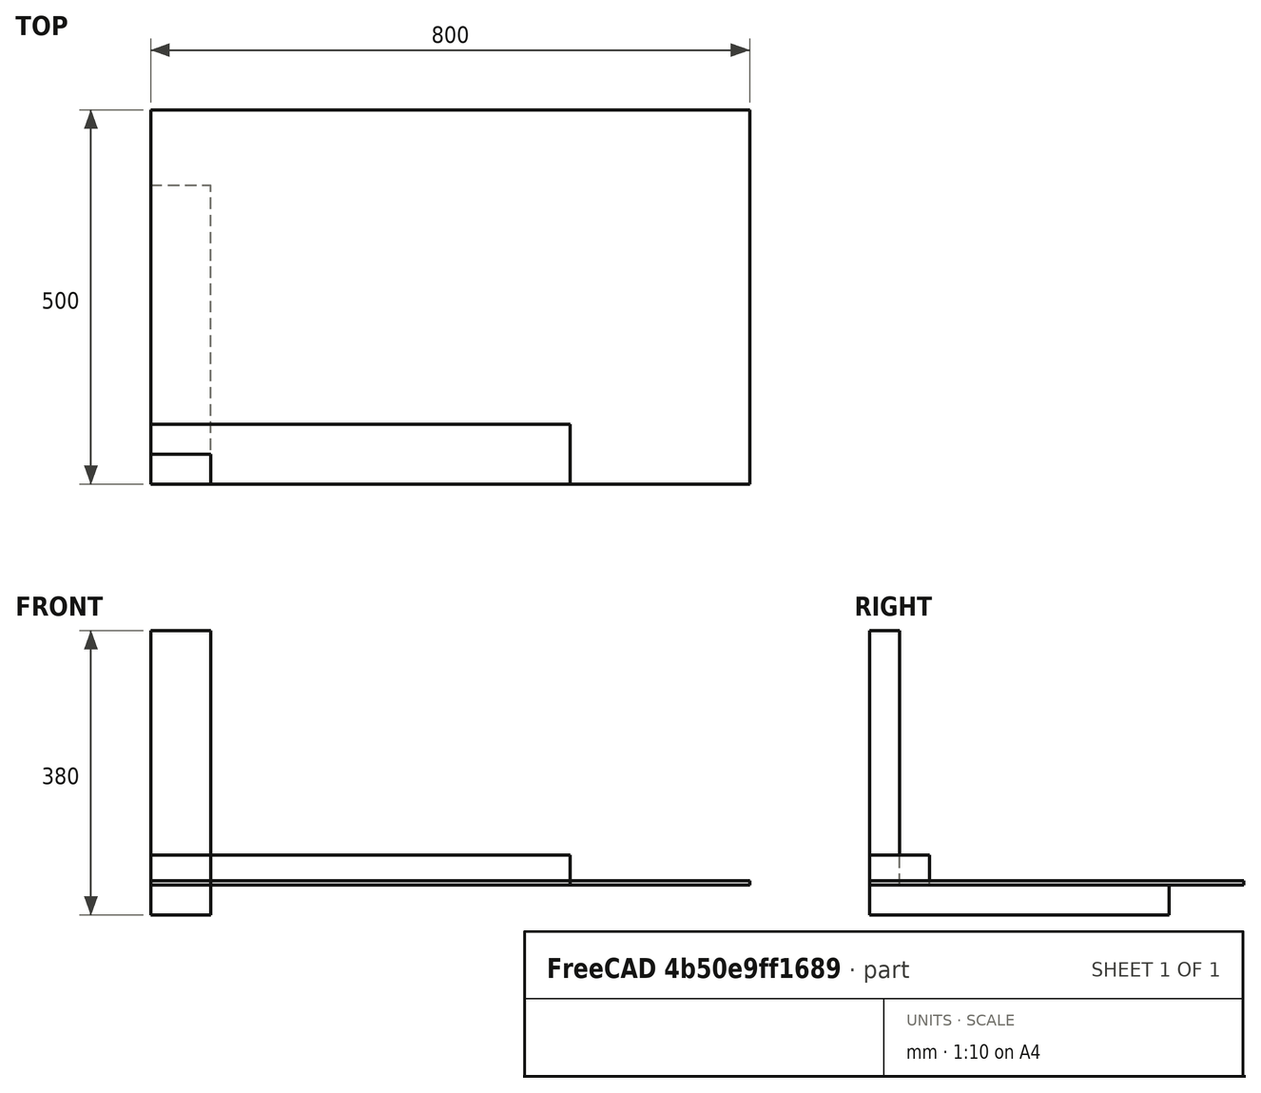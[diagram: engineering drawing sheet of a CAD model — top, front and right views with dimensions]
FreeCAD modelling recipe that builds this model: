
FCSTD DOCUMENT  (FreeCAD 0.21R33694 (Git))
Label: Lumber_coffe_table
Comment: Parametric design with spreadsheet.
License: Creative Commons Attribution-NonCommercial-ShareAlike 4.0
LicenseURL: https://creativecommons.org/licenses/by-nc-sa/4.0/
objects: PartDesign::AdditiveBox×4, PartDesign::Body×4, App::Link×4, App::Part×4, Spreadsheet::Sheet×1
note: 12 computed .brp shape members not serialized (recipe doc carries the construction recipe); baked Part::Feature solids carry a one-line shape summary decoded from their .brp

FEATURE [PartDesign::AdditiveBox] Box
  AttacherType = Attacher::AttachEngine3D
  Height = 340
  Length = 80
  MapMode = 1
  Width = 40
  expr: Height = Spreadsheet.l_v
  expr: Length = Spreadsheet.ancho
  expr: Width = Spreadsheet.grosor
FEATURE [PartDesign::Body] Body  label="Madera_300"
  Group = -> [Box]
  Origin = -> Origin001
  Tip = -> Box
FEATURE [PartDesign::AdditiveBox] Box001
  AttacherType = Attacher::AttachEngine3D
  Height = 400
  Length = 80
  Width = 40
  expr: Height = Spreadsheet.l_h
  expr: Length = Spreadsheet.ancho
  expr: Width = Spreadsheet.grosor
FEATURE [PartDesign::Body] Body001  label="Madera_500"
  Group = -> [Box001]
  Origin = -> Origin002
  Placement = pos=(0,0,0) rot=(-1,0,0;1.5708rad)
  Tip = -> Box001
FEATURE [App::Link] Link  label="Madera_501"
  LinkPlacement = pos=(0,0,380) rot=(0,0,1;0rad)
  LinkTransform = true
  LinkedObject = -> Body001
  Placement = pos=(0,0,380) rot=(0,0,1;0rad)
  expr: .LinkPlacement.Base.z = Spreadsheet.l_v + Spreadsheet.grosor
FEATURE [App::Link] Link001  label="Madera_502"
  LinkPlacement = pos=(0,360,0) rot=(0,0,1;0rad)
  LinkTransform = true
  LinkedObject = -> Body
  Placement = pos=(0,360,0) rot=(0,0,1;0rad)
  expr: .LinkPlacement.Base.y = Spreadsheet.l_h - Spreadsheet.grosor
FEATURE [App::Part] Part  label="Izquierda"
  Group = -> [Body001,Body,Link,Link001]
  Origin = -> Origin
FEATURE [App::Link] Link002  label="Derecha"
  LinkPlacement = pos=(640,0,0) rot=(0,0,1;0rad)
  LinkedObject = -> Part
  Placement = pos=(640,0,0) rot=(0,0,1;0rad)
  expr: .Placement.Base.x = Spreadsheet.l_u + Spreadsheet.ancho
FEATURE [PartDesign::AdditiveBox] Box002
  AttacherType = Attacher::AttachEngine3D
  Height = 40
  Length = 560
  Width = 80
  expr: Height = Spreadsheet.grosor
  expr: Length = Spreadsheet.l_u
  expr: Width = Spreadsheet.ancho
FEATURE [PartDesign::Body] Body002  label="Cuerpo"
  Group = -> [Box002]
  Origin = -> Origin004
  Tip = -> Box002
FEATURE [App::Part] Part001  label="Abajo"
  Group = -> [Body002]
  Origin = -> Origin003
  Placement = pos=(80,180,-40) rot=(0,0,1;0rad)
  expr: .Placement.Base.x = Spreadsheet.ancho
  expr: .Placement.Base.y = Spreadsheet.l_h / 2 - Spreadsheet.grosor / 2
  expr: .Placement.Base.z = -Spreadsheet.grosor
FEATURE [PartDesign::AdditiveBox] Box003
  AttacherType = Attacher::AttachEngine3D
  Height = 6
  Length = 800
  Width = 500
  expr: Height = Spreadsheet.cristal_grosor
  expr: Length = Spreadsheet.cristal_largo
  expr: Width = Spreadsheet.cristal_ancho
FEATURE [PartDesign::Body] Body003  label="Cuerpo001"
  Group = -> [Box003]
  Origin = -> Origin006
  Tip = -> Box003
FEATURE [App::Part] Part002  label="Cristal"
  Group = -> [Body003]
  Origin = -> Origin005
  Placement = pos=(-40,-50,380.1) rot=(0,0,1;0rad)
  expr: .Placement.Base.x = -(Spreadsheet.cristal_largo - (Spreadsheet.l_u + 2 * Spreadsheet.ancho)) / 2
  expr: .Placement.Base.y = -(Spreadsheet.cristal_ancho - Spreadsheet.l_h) / 2
  expr: .Placement.Base.z = Spreadsheet.l_v + Spreadsheet.grosor + 0.1 mm
FEATURE [Spreadsheet::Sheet] Spreadsheet
  cells = A1='Mesa de centro; A2='Mesa de centro con cristal; A6='Perfil de maderas; C6='Lumber profile; A7='Grosor; B7(grosor)==4 cm; C7='Thickness; A8='Ancho; B8(ancho)==8 cm; C8='Width; A11='Largos; C11='Lumbers; A12='Horizontales; B12(l_h)==40 cm; C12='Horizontal; A13='Verticales; B13(l_v)==34 cm; C13='Vertical; A14='Uniones; B14(l_u)==56 cm; C14='Unions; A16='Cristal; C16='Crystal; A17='Grosor; B17(cristal_grosor)==6 mm; C17='Thickness; A18='Largo; B18(cristal_largo)==80 cm; C18='Length; A19='Ancho; B19(cristal_ancho)==50 cm; C19='Width
FEATURE [App::Link] Link003  label="Arriba"
  LinkPlacement = pos=(80,180,340) rot=(0,0,1;0rad)
  LinkedObject = -> Part001
  Placement = pos=(80,180,340) rot=(0,0,1;0rad)
  expr: .Placement.Base.x = Spreadsheet.ancho
  expr: .Placement.Base.y = Spreadsheet.l_h / 2 - Spreadsheet.grosor / 2
  expr: .Placement.Base.z = Spreadsheet.l_v
FEATURE [App::Part] Part003  label="Coffee table"
  Group = -> [Part,Link002,Part001,Link003,Part002]
  Origin = -> Origin007
